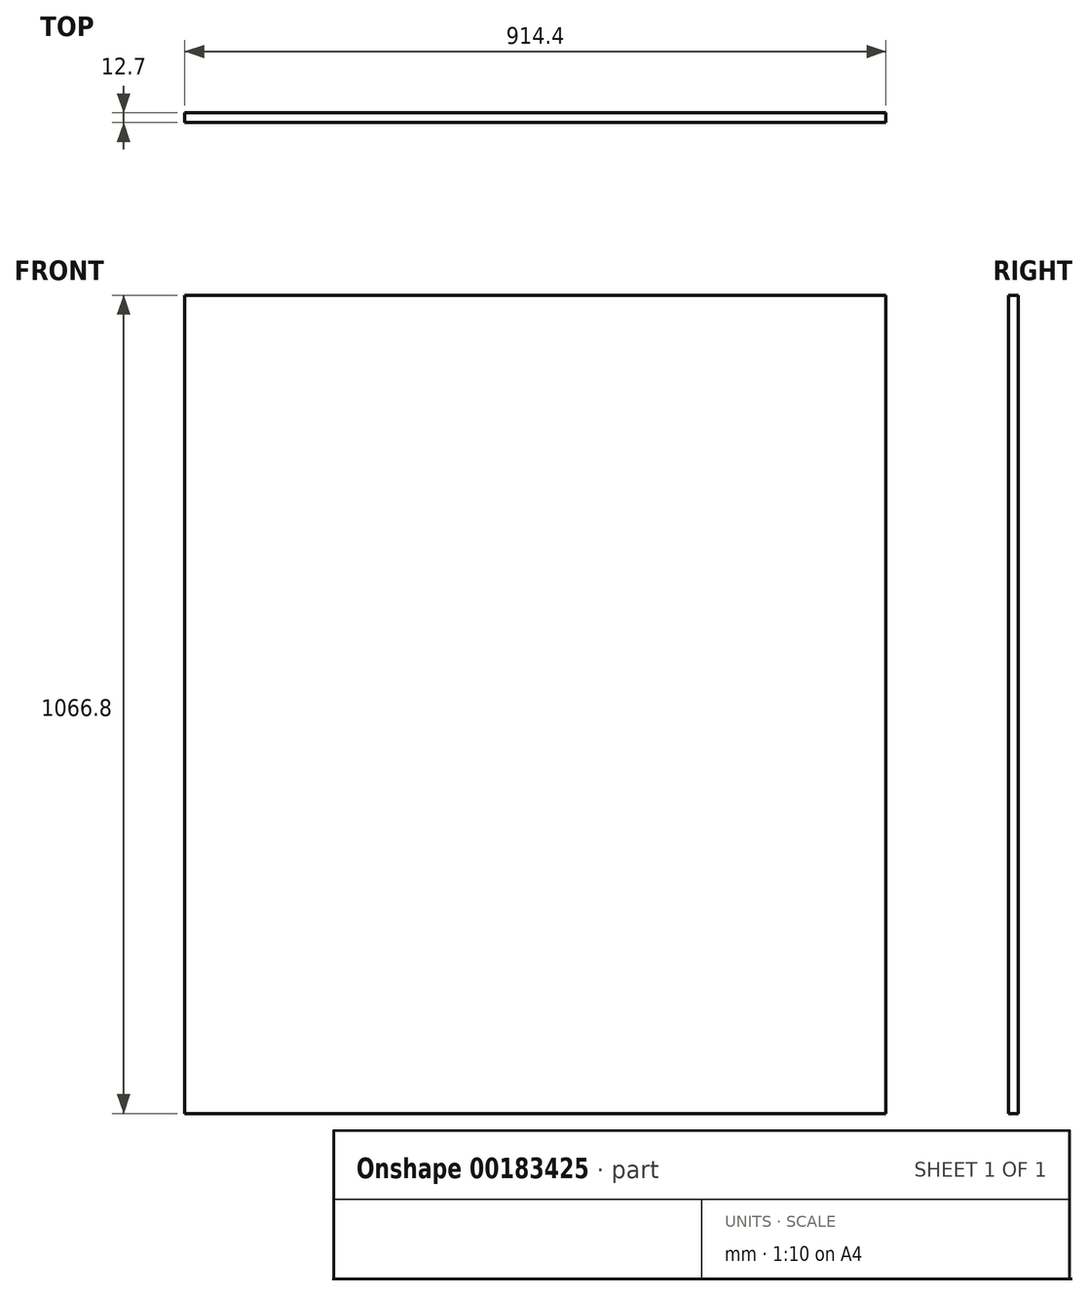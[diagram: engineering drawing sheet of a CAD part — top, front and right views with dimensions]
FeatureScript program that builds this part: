
annotation { "Feature Type Name" : "Feature", "Feature Type Description" : "" }
export const myFeature = defineFeature(function(context is Context, id is Id, definition is map)
    precondition{}
    {
        {
            var Q0;
            Q0=qCreatedBy(makeId("Front.planeOp"),FACE);
            var sketch = newSketch(context, id + "F0", { "sketchPlane" : qUnion([Q0])});
            skLineSegment(sketch, "E0.bottom", {"start": v(0, 0) * mm, "end": v(914.4, 0) * mm});
            skLineSegment(sketch, "E0.top", {"start": v(0, 1066.8) * mm, "end": v(914.4, 1066.8) * mm});
            skLineSegment(sketch, "E0.left", {"start": v(0, 0) * mm, "end": v(0, 1066.8) * mm});
            skLineSegment(sketch, "E0.right", {"start": v(914.4, 0) * mm, "end": v(914.4, 1066.8) * mm});
            skSolve(sketch);
        }
        {
            var Q0;
            Q0=makeQuery(id+"F0.imprint","IMPRINT",FACE,{"disambiguationData":[TD([[makeQuery(id+"F0.imprint","IMPRINT",EDGE,{"derivedFrom":sQuery(id+"F0.wireOp",EDGE,"E0.bottom")}),1.0]])]});
            extrude(context, id + "F1", {"entities" : qUnion([Q0]), "depth" : 12.7 * mm});
        }
    });
